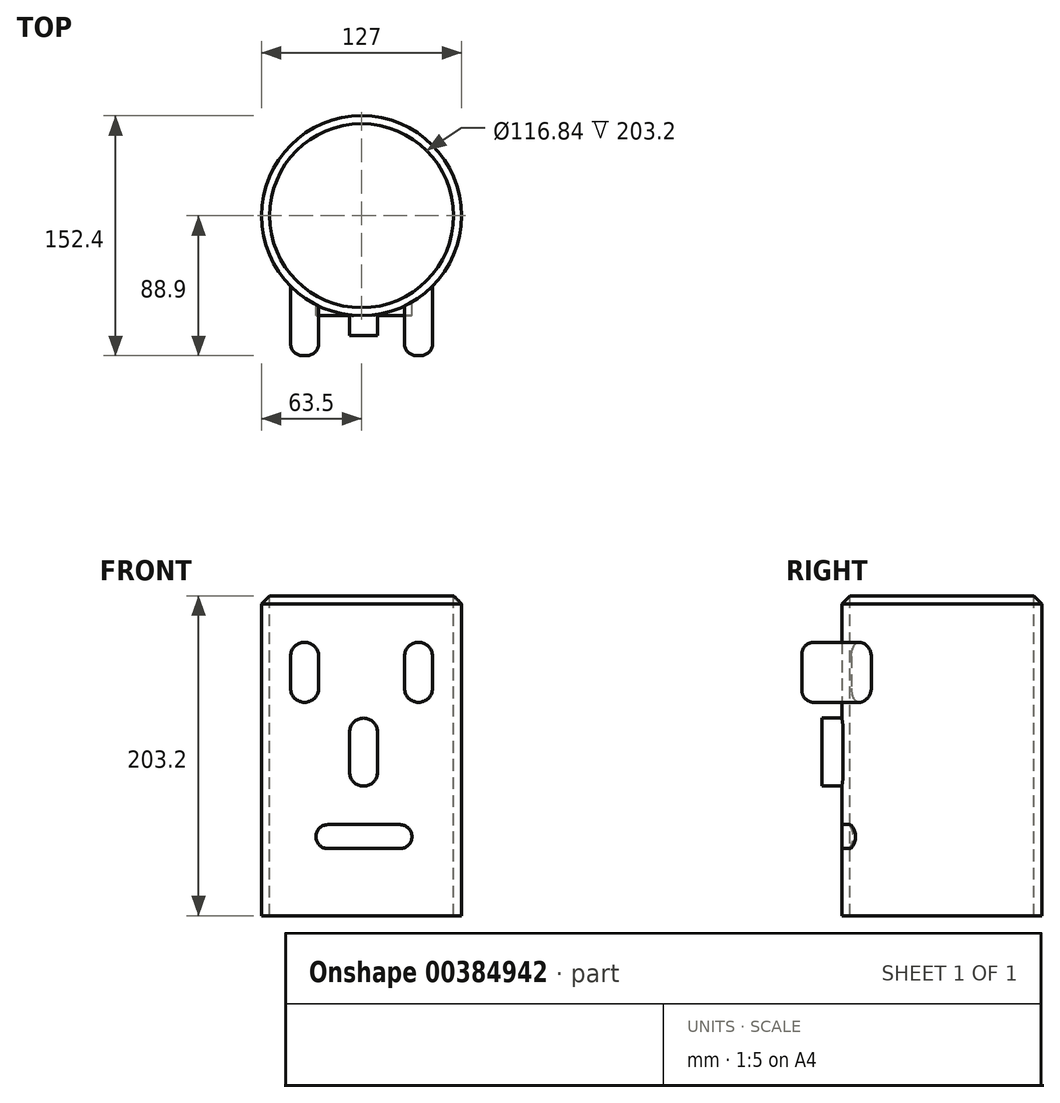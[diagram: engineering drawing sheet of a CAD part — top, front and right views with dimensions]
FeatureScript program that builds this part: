
annotation { "Feature Type Name" : "Feature", "Feature Type Description" : "" }
export const myFeature = defineFeature(function(context is Context, id is Id, definition is map)
    precondition{}
    {
        {
            var Q0;
            Q0=qCreatedBy(makeId("Top.planeOp"),FACE);
            var sketch = newSketch(context, id + "F0", { "sketchPlane" : qUnion([Q0])});
            skCircle(sketch, "E0", {"center": v(0, 0) * mm, "radius": 63.5 * mm});
            skSolve(sketch);
        }
        {
            var Q0;
            Q0=makeQuery(id+"F0.imprint","IMPRINT",FACE,{"disambiguationData":[TD([[makeQuery(id+"F0.imprint","IMPRINT",EDGE,{"derivedFrom":sQuery(id+"F0.wireOp",EDGE,"E0")}),1.0]])]});
            extrude(context, id + "F1", {"entities" : qUnion([Q0]), "endBound" : BoundingType.SYMMETRIC, "depth" : 203.2 * mm});
        }
        {
            var Q0;
            Q0=makeQuery(id+"F1.opExtrude","CAP_EDGE",EDGE,{"disambiguationData":[OSD([sQuery(id+"F0.wireOp",EDGE,"E0")])],"isStart":false});
            chamfer(context, id + "F2", {"entities" : qUnion([Q0]), "width" : 5.08 * mm, "tangentPropagation" : true});
        }
        {
            var Q0;
            Q0=qCreatedBy(makeId("Front.planeOp"),FACE);
            var sketch = newSketch(context, id + "F3", { "sketchPlane" : qUnion([Q0])});
            skLineSegment(sketch, "E1", {"start": v(-45.07, 63.16) * mm, "end": v(-45.07, 42.84) * mm});
            skLineSegment(sketch, "E2", {"start": v(-27.3, 63.16) * mm, "end": v(-27.3, 42.84) * mm});
            skLineSegment(sketch, "E3", {"start": v(27.3, 63.16) * mm, "end": v(27.3, 42.84) * mm});
            skLineSegment(sketch, "E4", {"start": v(45.07, 42.84) * mm, "end": v(45.07, 63.16) * mm});
            skArc(sketch, "E5", {"start": v(-45.07, 63.16) * mm, "mid": v(-36.18, 72.05) * mm, "end": v(-27.3, 63.16) * mm});
            skArc(sketch, "E6", {"start": v(-27.3, 42.84) * mm, "mid": v(-36.18, 33.95) * mm, "end": v(-45.07, 42.84) * mm});
            skArc(sketch, "E7", {"start": v(27.3, 42.84) * mm, "mid": v(36.18, 33.96) * mm, "end": v(45.07, 42.84) * mm});
            skArc(sketch, "E8", {"start": v(45.07, 63.16) * mm, "mid": v(36.18, 72.05) * mm, "end": v(27.3, 63.16) * mm});
            skLineSegment(sketch, "E9", {"start": v(-27.3, 42.84) * mm, "end": v(0, 0) * mm, "construction": true});
            skLineSegment(sketch, "E10", {"start": v(0, 0) * mm, "end": v(27.3, 42.84) * mm, "construction": true});
            skSolve(sketch);
        }
        {
            var Q0;
            Q0=makeQuery(id+"F3.imprint","IMPRINT",FACE,{"disambiguationData":[TD([[makeQuery(id+"F3.imprint","IMPRINT",EDGE,{"derivedFrom":sQuery(id+"F3.wireOp",EDGE,"E1")}),1.0]])]});
            var Q1;
            Q1=makeQuery(id+"F3.imprint","IMPRINT",FACE,{"disambiguationData":[TD([[makeQuery(id+"F3.imprint","IMPRINT",EDGE,{"derivedFrom":sQuery(id+"F3.wireOp",EDGE,"E3")}),1.0]])]});
            extrude(context, id + "F4", {"entities" : qUnion([Q0, Q1]), "operationType" : NewBodyOperationType.ADD, "depth" : 88.9 * mm});
        }
        {
            var Q0;
            Q0=qCreatedBy(makeId("Front.planeOp"),FACE);
            var sketch = newSketch(context, id + "F5", { "sketchPlane" : qUnion([Q0])});
            skLineSegment(sketch, "E11", {"start": v(-7.61, 14.99) * mm, "end": v(-7.61, -10.41) * mm});
            skLineSegment(sketch, "E12", {"start": v(10.17, -10.41) * mm, "end": v(10.17, 14.99) * mm});
            skArc(sketch, "E13", {"start": v(-7.61, 14.99) * mm, "mid": v(1.28, 23.88) * mm, "end": v(10.17, 14.99) * mm});
            skArc(sketch, "E14", {"start": v(10.17, -10.41) * mm, "mid": v(1.28, -19.3) * mm, "end": v(-7.61, -10.41) * mm});
            skSolve(sketch);
        }
        {
            var Q0;
            Q0=makeQuery(id+"F5.imprint","IMPRINT",FACE,{"disambiguationData":[TD([[makeQuery(id+"F5.imprint","IMPRINT",EDGE,{"derivedFrom":sQuery(id+"F5.wireOp",EDGE,"E11")}),1.0]])]});
            extrude(context, id + "F6", {"entities" : qUnion([Q0]), "operationType" : NewBodyOperationType.ADD, "depth" : 76.2 * mm});
        }
        {
            var Q0;
            Q0=qCreatedBy(makeId("Front.planeOp"),FACE);
            var sketch = newSketch(context, id + "F7", { "sketchPlane" : qUnion([Q0])});
            skLineSegment(sketch, "E15", {"start": v(-21.37, -43.74) * mm, "end": v(24.35, -43.74) * mm});
            skLineSegment(sketch, "E16", {"start": v(24.35, -58.98) * mm, "end": v(-21.37, -58.98) * mm});
            skArc(sketch, "E17", {"start": v(-21.37, -43.74) * mm, "mid": v(-29, -51.36) * mm, "end": v(-21.37, -58.98) * mm});
            skArc(sketch, "E18", {"start": v(24.35, -43.74) * mm, "mid": v(31.97, -51.36) * mm, "end": v(24.35, -58.98) * mm});
            skSolve(sketch);
        }
        {
            var Q0;
            Q0=makeQuery(id+"F7.imprint","IMPRINT",FACE,{"disambiguationData":[TD([[makeQuery(id+"F7.imprint","IMPRINT",EDGE,{"derivedFrom":sQuery(id+"F7.wireOp",EDGE,"E15")}),-1.0]])]});
            extrude(context, id + "F8", {"entities" : qUnion([Q0]), "operationType" : NewBodyOperationType.ADD, "depth" : 63.5 * mm});
        }
        {
            var Q0;
            Q0=makeQuery(id+"F1.opExtrude","CAP_FACE",FACE,{"disambiguationData":[OSD([sQuery(id+"F0.wireOp",EDGE,"E0")])],"isStart":false});
            var Q1;
            Q1=makeQuery(id+"F1.opExtrude","CAP_FACE",FACE,{"disambiguationData":[OSD([sQuery(id+"F0.wireOp",EDGE,"E0")])],"isStart":true});
            extrude(context, id + "F9", {"entities" : qUnion([Q0]), "operationType" : NewBodyOperationType.REMOVE, "endBound" : BoundingType.UP_TO_SURFACE, "oppositeDirection" : true, "endBoundEntityFace" : qUnion([Q1]), "depth" : 25.4 * mm});
        }
        {
            var Q0;
            Q0=qCreatedBy(makeId("Top.planeOp"),FACE);
            var Q1;
            Q1=makeQuery(id+"F4.opExtrude","CAP_VERTEX",VERTEX,{"disambiguationData":[OSD([sQuery(id+"F3.wireOp",EDGE,"E1"),sQuery(id+"F3.wireOp",EDGE,"E5")])],"isStart":false});
            cPlane(context, id + "F10", {"entities" : qUnion([Q0, Q1]), "cplaneType" : CPlaneType.PLANE_POINT, "offset" : 25.4 * mm, "width" : 152.4 * mm, "height" : 152.4 * mm});
        }
        {
            var Q0;
            Q0=makeQuery(id+"F4.opExtrude","CAP_EDGE",EDGE,{"disambiguationData":[OSD([sQuery(id+"F3.wireOp",EDGE,"E5")])],"isStart":false});
            var Q1;
            Q1=makeQuery(id+"F4.opExtrude","CAP_EDGE",EDGE,{"disambiguationData":[OSD([sQuery(id+"F3.wireOp",EDGE,"E2")])],"isStart":false});
            var Q2;
            Q2=makeQuery(id+"F4.opExtrude","CAP_EDGE",EDGE,{"disambiguationData":[OSD([sQuery(id+"F3.wireOp",EDGE,"E7")])],"isStart":false});
            var Q3;
            Q3=makeQuery(id+"F4.opExtrude","CAP_EDGE",EDGE,{"disambiguationData":[OSD([sQuery(id+"F3.wireOp",EDGE,"E3")])],"isStart":false});
            fillet(context, id + "F11", {"entities" : qUnion([Q0, Q1, Q2, Q3]), "radius" : 7.62 * mm, "tangentPropagation" : true, "allowEdgeOverflow" : false});
        }
    });
